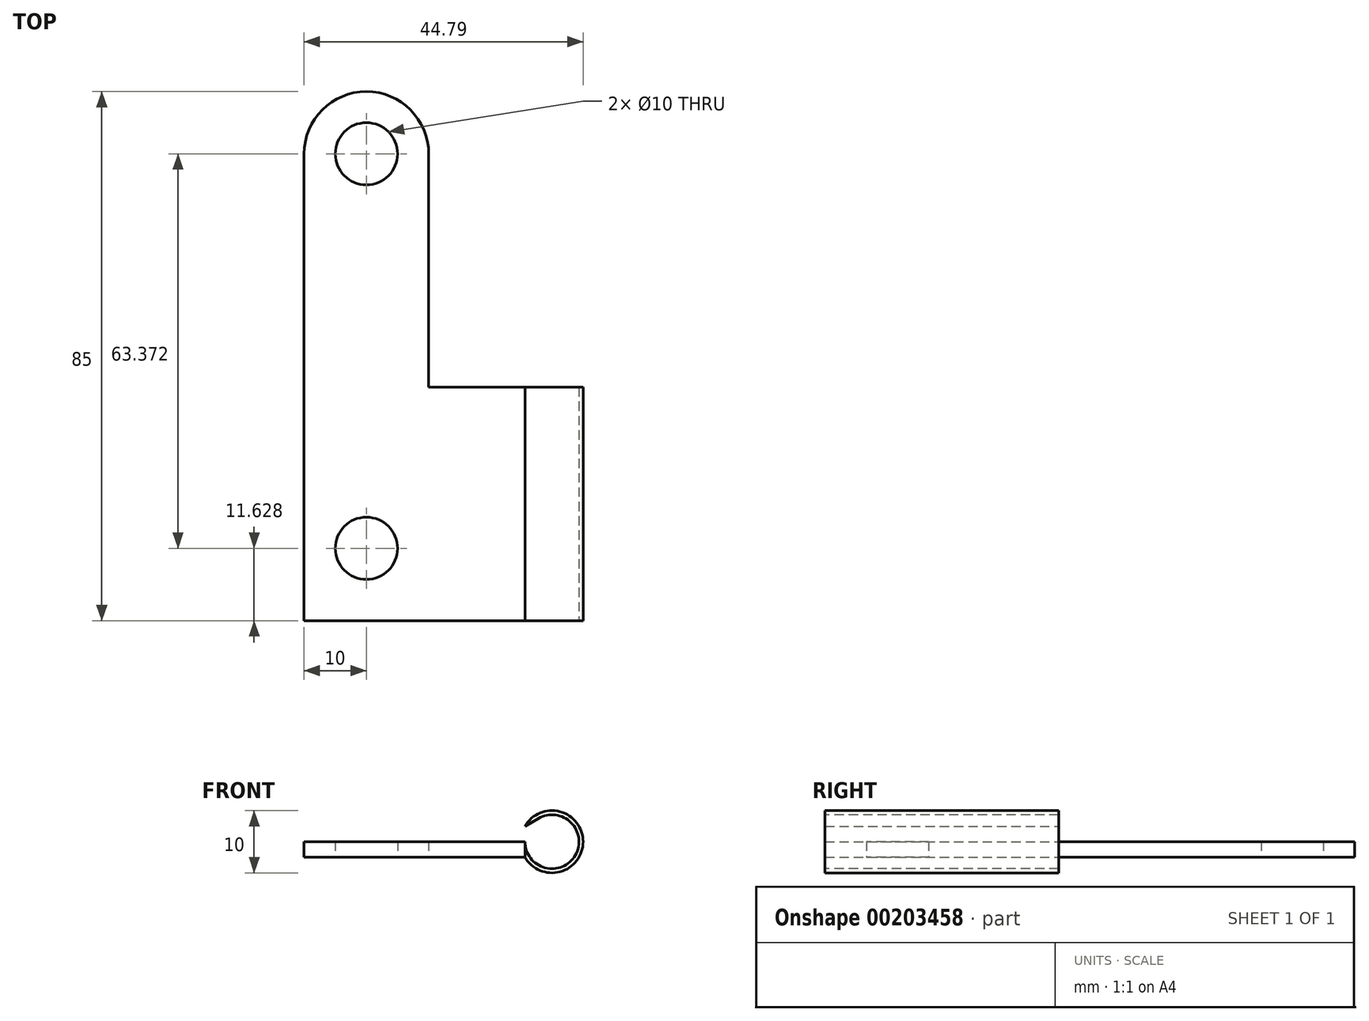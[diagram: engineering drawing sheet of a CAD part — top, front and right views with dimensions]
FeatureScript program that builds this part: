
annotation { "Feature Type Name" : "Feature", "Feature Type Description" : "" }
export const myFeature = defineFeature(function(context is Context, id is Id, definition is map)
    precondition{}
    {
        {
            var Q0;
            Q0=qCreatedBy(makeId("Top.planeOp"),FACE);
            var sketch = newSketch(context, id + "F0", { "sketchPlane" : qUnion([Q0])});
            skLineSegment(sketch, "E0.bottom", {"start": v(0, 0) * mm, "end": v(20, 0) * mm});
            skLineSegment(sketch, "E0.top", {"start": v(0, 75) * mm, "end": v(20, 75) * mm});
            skLineSegment(sketch, "E0.left", {"start": v(0, 0) * mm, "end": v(0, 75) * mm});
            skLineSegment(sketch, "E0.right", {"start": v(20, 0) * mm, "end": v(20, 75) * mm});
            skCircle(sketch, "E1", {"center": v(10, 75) * mm, "radius": 10 * mm});
            skLineSegment(sketch, "E2.bottom", {"start": v(20, 0) * mm, "end": v(35.46, 0) * mm});
            skLineSegment(sketch, "E2.top", {"start": v(20, 37.5) * mm, "end": v(35.46, 37.5) * mm});
            skLineSegment(sketch, "E2.left", {"start": v(20, 0) * mm, "end": v(20, 37.5) * mm});
            skLineSegment(sketch, "E2.right", {"start": v(35.46, 0) * mm, "end": v(35.46, 37.5) * mm});
            skCircle(sketch, "E3", {"center": v(10, 75) * mm, "radius": 5 * mm});
            skCircle(sketch, "E4", {"center": v(10, 11.63) * mm, "radius": 5 * mm});
            skSolve(sketch);
        }
        {
            var Q0;
            Q0=qSketchRegion(id+"F0",true);
            extrude(context, id + "F1", {"entities" : qUnion([Q0]), "depth" : 2.5 * mm});
        }
        {
            var Q0;
            Q0=makeQuery(id+"F1.opExtrude","SWEPT_FACE",FACE,{"disambiguationData":[OSD([sQuery(id+"F0.wireOp",EDGE,"E2.top")])]});
            var sketch = newSketch(context, id + "F2", { "sketchPlane" : qUnion([Q0])});
            skPoint(sketch, "E5.startSnap0", {"position": v(-35.46, 1.25) * mm});
            skArc(sketch, "E6", {"start": v(-35.46, 0) * mm, "mid": v(-44.79, 2.5) * mm, "end": v(-35.46, 5) * mm});
            skSolve(sketch);
        }
        {
            var Q0;
            Q0=makeQuery(id+"F1.opExtrude","SWEPT_FACE",FACE,{"disambiguationData":[OSD([sQuery(id+"F0.wireOp",EDGE,"E2.right")])]});
            var Q1;
            Q1=sQuery(id+"F2.wireOp",EDGE,"kZosnaDB-Kpzb-LAQg-lEwK-jwXfYmuygm6T");
            var Q2;
            Q2=sQuery(id+"F2.wireOp",EDGE,"E6");
            sweep(context, id + "F3", {"profiles" : qUnion([Q0]), "path" : qUnion([Q1, Q2])});
        }
    });
